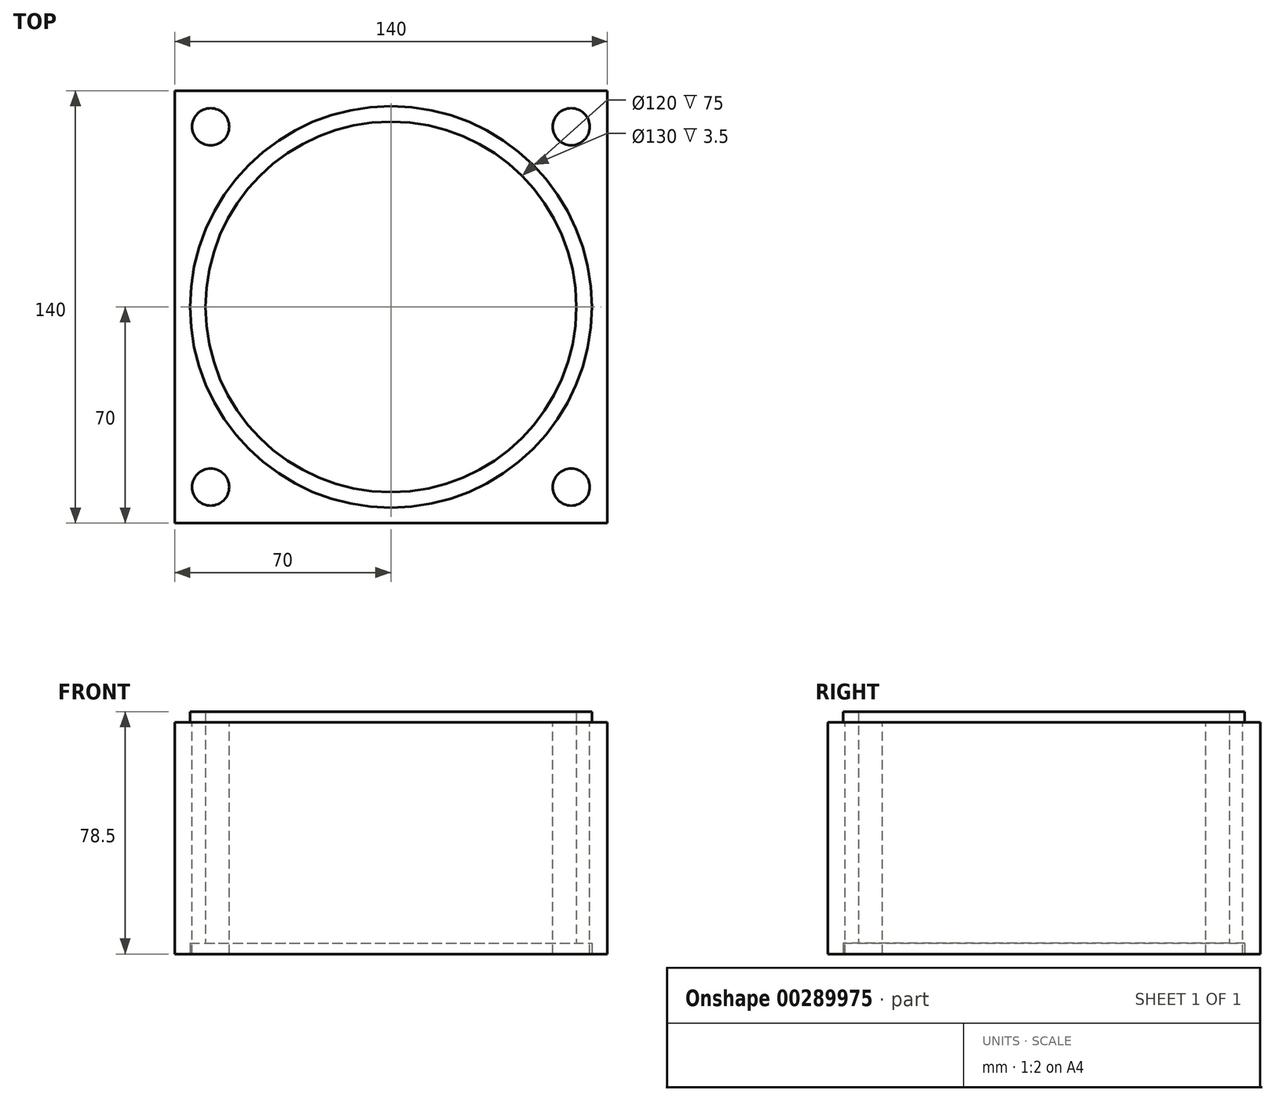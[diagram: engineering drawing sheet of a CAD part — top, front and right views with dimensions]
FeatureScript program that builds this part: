
annotation { "Feature Type Name" : "Feature", "Feature Type Description" : "" }
export const myFeature = defineFeature(function(context is Context, id is Id, definition is map)
    precondition{}
    {
        {
            var Q0;
            Q0=qCreatedBy(makeId("Top.planeOp"),FACE);
            var sketch = newSketch(context, id + "F0", { "sketchPlane" : qUnion([Q0])});
            skLineSegment(sketch, "E0.bottom", {"start": v(-70, 70) * mm, "end": v(70, 70) * mm});
            skLineSegment(sketch, "E0.top", {"start": v(-70, -70) * mm, "end": v(70, -70) * mm});
            skLineSegment(sketch, "E0.left", {"start": v(-70, 70) * mm, "end": v(-70, -70) * mm});
            skLineSegment(sketch, "E0.right", {"start": v(70, 70) * mm, "end": v(70, -70) * mm});
            skCircle(sketch, "E1", {"center": v(0, 0) * mm, "radius": 60 * mm});
            skSolve(sketch);
        }
        {
            var Q0;
            Q0=qSketchRegion(id+"F0",true);
            extrude(context, id + "F1", {"entities" : qUnion([Q0]), "depth" : 75 * mm});
        }
        {
            var Q0;
            Q0=makeQuery(id+"F1.opExtrude","CAP_FACE",FACE,{"disambiguationData":[OSD([sQuery(id+"F0.wireOp",EDGE,"E0.bottom"),sQuery(id+"F0.wireOp",EDGE,"E0.top"),sQuery(id+"F0.wireOp",EDGE,"E0.left"),sQuery(id+"F0.wireOp",EDGE,"E0.right"),sQuery(id+"F0.wireOp",EDGE,"E1")])],"isStart":false});
            var sketch = newSketch(context, id + "F2", { "sketchPlane" : qUnion([Q0])});
            skCircle(sketch, "E2", {"center": v(0, 0) * mm, "radius": 65 * mm});
            skCircle(sketch, "E3", {"center": v(0, 0) * mm, "radius": 60 * mm});
            skSolve(sketch);
        }
        {
            var Q0;
            Q0=qSketchRegion(id+"F2",true);
            extrude(context, id + "F3", {"entities" : qUnion([Q0]), "operationType" : NewBodyOperationType.ADD, "depth" : 3.5 * mm});
        }
        {
            var Q0;
            Q0=makeQuery(id+"F1.opExtrude","CAP_FACE",FACE,{"disambiguationData":[OSD([sQuery(id+"F0.wireOp",EDGE,"E0.bottom"),sQuery(id+"F0.wireOp",EDGE,"E0.top"),sQuery(id+"F0.wireOp",EDGE,"E0.left"),sQuery(id+"F0.wireOp",EDGE,"E0.right"),sQuery(id+"F0.wireOp",EDGE,"E1")])],"isStart":true});
            var sketch = newSketch(context, id + "F4", { "sketchPlane" : qUnion([Q0])});
            skCircle(sketch, "E4", {"center": v(0, 0) * mm, "radius": 65 * mm});
            skCircle(sketch, "E5", {"center": v(0, 0) * mm, "radius": 50 * mm});
            skSolve(sketch);
        }
        {
            var Q0;
            Q0=qSketchRegion(id+"F4",true);
            extrude(context, id + "F5", {"entities" : qUnion([Q0]), "operationType" : NewBodyOperationType.REMOVE, "oppositeDirection" : true, "depth" : 3.5 * mm});
        }
        {
            var Q0;
            Q0=makeQuery(id+"F1.opExtrude","CAP_FACE",FACE,{"disambiguationData":[OSD([sQuery(id+"F0.wireOp",EDGE,"E0.bottom"),sQuery(id+"F0.wireOp",EDGE,"E0.top"),sQuery(id+"F0.wireOp",EDGE,"E0.left"),sQuery(id+"F0.wireOp",EDGE,"E0.right"),sQuery(id+"F0.wireOp",EDGE,"E1")])],"isStart":false});
            var sketch = newSketch(context, id + "F6", { "sketchPlane" : qUnion([Q0])});
            skCircle(sketch, "E6", {"center": v(0, 0) * mm, "radius": 82.5 * mm});
            skLineSegment(sketch, "E7", {"start": v(0, 0) * mm, "end": v(-70, 70) * mm});
            skCircle(sketch, "E8", {"center": v(-58.34, 58.34) * mm, "radius": 6 * mm});
            skCircle(sketch, "E9.1.0", {"center": v(-58.34, -58.34) * mm, "radius": 6 * mm});
            skCircle(sketch, "E9.2.0", {"center": v(58.34, -58.34) * mm, "radius": 6 * mm});
            skCircle(sketch, "E9.3.0", {"center": v(58.34, 58.34) * mm, "radius": 6 * mm});
            skLineSegment(sketch, "E9.anchor1", {"start": v(0, 0) * mm, "end": v(-58.34, 58.34) * mm, "construction": true});
            skLineSegment(sketch, "E9.anchor2", {"start": v(0, 0) * mm, "end": v(58.34, 58.34) * mm, "construction": true});
            skSolve(sketch);
        }
        {
            var Q0;
            {var subQ0=sQuery(id+"F6.wireOp",EDGE,"E8");var subQ1=sQuery(id+"F6.wireOp",EDGE,"E6");var subQ2=makeQuery(id+"F6.imprint","INTERSECT",VERTEX,{"disambiguationData":[OD(0.0)],"derivedFrom":[subQ1,subQ0]});Q0=makeQuery(id+"F6.imprint","IMPRINT",FACE,{"disambiguationData":[TD([[makeQuery(id+"F6.imprint","IMPRINT",EDGE,{"disambiguationData":[TD([[subQ2,-1.0]])],"derivedFrom":subQ1}),-1.0]])]});}
            var Q1;
            {var subQ0=sQuery(id+"F6.wireOp",EDGE,"E8");var subQ1=sQuery(id+"F6.wireOp",EDGE,"E6");var subQ2=makeQuery(id+"F6.imprint","INTERSECT",VERTEX,{"disambiguationData":[OD(0.0)],"derivedFrom":[subQ1,subQ0]});Q1=makeQuery(id+"F6.imprint","IMPRINT",FACE,{"disambiguationData":[TD([[makeQuery(id+"F6.imprint","IMPRINT",EDGE,{"disambiguationData":[TD([[subQ2,-1.0]])],"derivedFrom":subQ1}),1.0]])]});}
            var Q2;
            {var subQ0=sQuery(id+"F6.wireOp",EDGE,"E7");var subQ1=sQuery(id+"F6.wireOp",EDGE,"E6");var subQ2=makeQuery(id+"F6.imprint","INTERSECT",VERTEX,{"derivedFrom":[subQ1,subQ0]});Q2=makeQuery(id+"F6.imprint","IMPRINT",FACE,{"disambiguationData":[TD([[makeQuery(id+"F6.imprint","IMPRINT",EDGE,{"disambiguationData":[TD([[subQ2,-1.0]])],"derivedFrom":subQ1}),1.0]])]});}
            var Q3;
            {var subQ0=sQuery(id+"F6.wireOp",EDGE,"E7");var subQ1=sQuery(id+"F6.wireOp",EDGE,"E6");var subQ2=makeQuery(id+"F6.imprint","INTERSECT",VERTEX,{"derivedFrom":[subQ1,subQ0]});Q3=makeQuery(id+"F6.imprint","IMPRINT",FACE,{"disambiguationData":[TD([[makeQuery(id+"F6.imprint","IMPRINT",EDGE,{"disambiguationData":[TD([[subQ2,-1.0]])],"derivedFrom":subQ1}),-1.0]])]});}
            var Q4;
            {var subQ0=sQuery(id+"F6.wireOp",EDGE,"E9.3.0");var subQ1=sQuery(id+"F6.wireOp",EDGE,"E6");var subQ2=makeQuery(id+"F6.imprint","INTERSECT",VERTEX,{"disambiguationData":[OD(0.0)],"derivedFrom":[subQ1,subQ0]});Q4=makeQuery(id+"F6.imprint","IMPRINT",FACE,{"disambiguationData":[TD([[makeQuery(id+"F6.imprint","IMPRINT",EDGE,{"disambiguationData":[TD([[subQ2,-1.0]])],"derivedFrom":subQ1}),-1.0]])]});}
            var Q5;
            {var subQ0=sQuery(id+"F6.wireOp",EDGE,"E9.3.0");var subQ1=sQuery(id+"F6.wireOp",EDGE,"E6");var subQ2=makeQuery(id+"F6.imprint","INTERSECT",VERTEX,{"disambiguationData":[OD(0.0)],"derivedFrom":[subQ1,subQ0]});Q5=makeQuery(id+"F6.imprint","IMPRINT",FACE,{"disambiguationData":[TD([[makeQuery(id+"F6.imprint","IMPRINT",EDGE,{"disambiguationData":[TD([[subQ2,-1.0]])],"derivedFrom":subQ1}),1.0]])]});}
            var Q6;
            {var subQ0=sQuery(id+"F6.wireOp",EDGE,"E9.2.0");var subQ1=sQuery(id+"F6.wireOp",EDGE,"E6");var subQ2=makeQuery(id+"F6.imprint","INTERSECT",VERTEX,{"disambiguationData":[OD(0.0)],"derivedFrom":[subQ1,subQ0]});Q6=makeQuery(id+"F6.imprint","IMPRINT",FACE,{"disambiguationData":[TD([[makeQuery(id+"F6.imprint","IMPRINT",EDGE,{"disambiguationData":[TD([[subQ2,-1.0]])],"derivedFrom":subQ1}),-1.0]])]});}
            var Q7;
            {var subQ0=sQuery(id+"F6.wireOp",EDGE,"E9.2.0");var subQ1=sQuery(id+"F6.wireOp",EDGE,"E6");var subQ2=makeQuery(id+"F6.imprint","INTERSECT",VERTEX,{"disambiguationData":[OD(0.0)],"derivedFrom":[subQ1,subQ0]});Q7=makeQuery(id+"F6.imprint","IMPRINT",FACE,{"disambiguationData":[TD([[makeQuery(id+"F6.imprint","IMPRINT",EDGE,{"disambiguationData":[TD([[subQ2,-1.0]])],"derivedFrom":subQ1}),1.0]])]});}
            var Q8;
            {var subQ0=sQuery(id+"F6.wireOp",EDGE,"E9.1.0");var subQ1=sQuery(id+"F6.wireOp",EDGE,"E6");var subQ2=makeQuery(id+"F6.imprint","INTERSECT",VERTEX,{"disambiguationData":[OD(0.0)],"derivedFrom":[subQ1,subQ0]});Q8=makeQuery(id+"F6.imprint","IMPRINT",FACE,{"disambiguationData":[TD([[makeQuery(id+"F6.imprint","IMPRINT",EDGE,{"disambiguationData":[TD([[subQ2,-1.0]])],"derivedFrom":subQ1}),-1.0]])]});}
            var Q9;
            {var subQ0=sQuery(id+"F6.wireOp",EDGE,"E9.1.0");var subQ1=sQuery(id+"F6.wireOp",EDGE,"E6");var subQ2=makeQuery(id+"F6.imprint","INTERSECT",VERTEX,{"disambiguationData":[OD(0.0)],"derivedFrom":[subQ1,subQ0]});Q9=makeQuery(id+"F6.imprint","IMPRINT",FACE,{"disambiguationData":[TD([[makeQuery(id+"F6.imprint","IMPRINT",EDGE,{"disambiguationData":[TD([[subQ2,-1.0]])],"derivedFrom":subQ1}),1.0]])]});}
            extrude(context, id + "F7", {"entities" : qUnion([Q0, Q1, Q2, Q3, Q4, Q5, Q6, Q7, Q8, Q9]), "operationType" : NewBodyOperationType.REMOVE, "endBound" : BoundingType.THROUGH_ALL, "oppositeDirection" : true, "depth" : 25 * mm});
        }
    });
